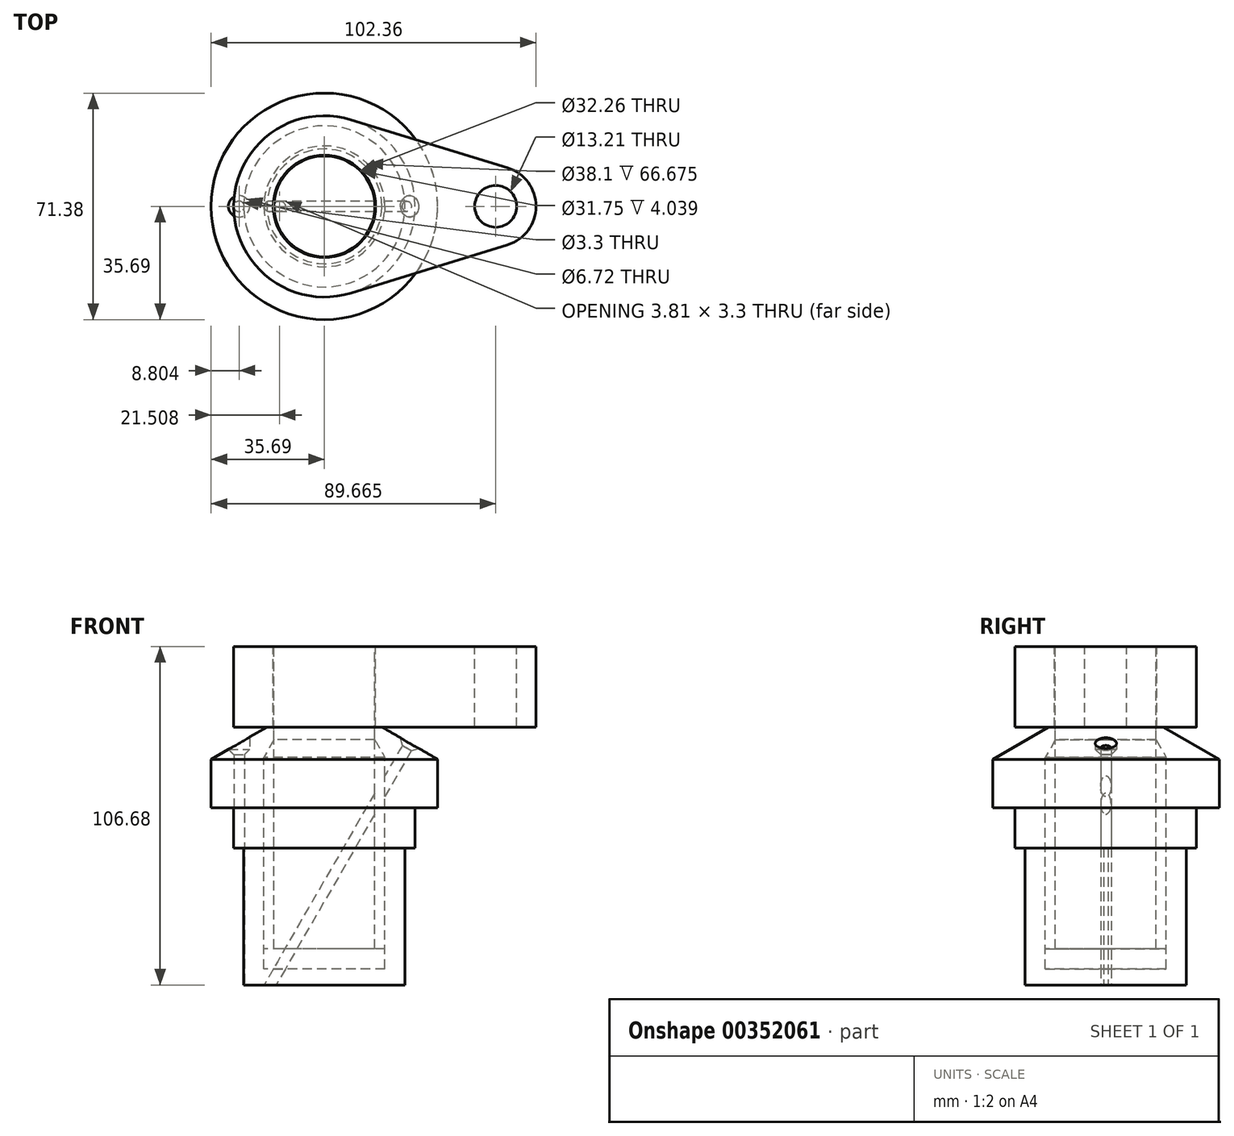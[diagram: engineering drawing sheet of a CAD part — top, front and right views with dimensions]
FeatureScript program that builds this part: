
annotation { "Feature Type Name" : "Feature", "Feature Type Description" : "" }
export const myFeature = defineFeature(function(context is Context, id is Id, definition is map)
    precondition{}
    {
        {
            var Q0;
            Q0=qCreatedBy(makeId("Front.planeOp"),FACE);
            var sketch = newSketch(context, id + "F0", { "sketchPlane" : qUnion([Q0])});
            skLineSegment(sketch, "E0", {"start": v(0, 0) * mm, "end": v(25.4, 0) * mm});
            skLineSegment(sketch, "E1", {"start": v(25.4, 0) * mm, "end": v(25.4, 43.2) * mm});
            skLineSegment(sketch, "E2", {"start": v(25.4, 43.2) * mm, "end": v(28.58, 43.2) * mm});
            skLineSegment(sketch, "E3", {"start": v(28.58, 43.2) * mm, "end": v(28.58, 55.9) * mm});
            skLineSegment(sketch, "E4", {"start": v(28.58, 55.9) * mm, "end": v(35.69, 55.9) * mm});
            skLineSegment(sketch, "E5", {"start": v(35.69, 55.9) * mm, "end": v(35.69, 71.13) * mm});
            skLineSegment(sketch, "E6", {"start": v(35.69, 71.13) * mm, "end": v(18.08, 81.3) * mm});
            skLineSegment(sketch, "E7", {"start": v(18.08, 81.3) * mm, "end": v(0, 81.3) * mm});
            skLineSegment(sketch, "E8", {"start": v(0, 81.3) * mm, "end": v(0, 0) * mm});
            skLineSegment(sketch, "E9", {"start": v(15.87, 81.3) * mm, "end": v(15.87, 77.25) * mm});
            skLineSegment(sketch, "E10", {"start": v(15.88, 77.25) * mm, "end": v(19.05, 71.75) * mm});
            skLineSegment(sketch, "E11", {"start": v(19.05, 71.75) * mm, "end": v(19.05, 5.08) * mm});
            skLineSegment(sketch, "E12", {"start": v(19.05, 5.08) * mm, "end": v(0, 5.08) * mm});
            skLineSegment(sketch, "E13", {"start": v(0, 89.12) * mm, "end": v(0, -8.25) * mm, "construction": true});
            skSolve(sketch);
        }
        {
            var Q0;
            {var subQ3=sQuery(id+"F0.wireOp",EDGE,"E0");Q0=makeQuery(id+"F0.imprint","IMPRINT",FACE,{"disambiguationData":[TD([[makeQuery(id+"F0.imprint","IMPRINT",EDGE,{"derivedFrom":subQ3}),1.0]])]});}
            var Q1;
            Q1=sQuery(id+"F0.wireOp",EDGE,"E8");
            revolve(context, id + "F1", {"entities" : qUnion([Q0]), "axis" : qUnion([Q1]), "revolveType" : RevolveType.FULL});
        }
        {
            var Q0;
            Q0=qCreatedBy(makeId("Front.planeOp"),FACE);
            var sketch = newSketch(context, id + "F2", { "sketchPlane" : qUnion([Q0])});
            skLineSegment(sketch, "E14.0", {"start": v(19.05, 5.08) * mm, "end": v(0, 5.08) * mm});
            skPoint(sketch, "E14.1", {"position": v(19.05, 11.43) * mm});
            skPoint(sketch, "E14.2", {"position": v(15.88, 77.25) * mm});
            skLineSegment(sketch, "E15", {"start": v(19.05, 5.08) * mm, "end": v(19.05, 11.43) * mm});
            skLineSegment(sketch, "E16", {"start": v(15.88, 11.43) * mm, "end": v(15.88, 106.68) * mm});
            skLineSegment(sketch, "E17", {"start": v(15.88, 106.68) * mm, "end": v(0, 106.68) * mm});
            skLineSegment(sketch, "E18", {"start": v(0, 106.68) * mm, "end": v(0, 5.08) * mm});
            skLineSegment(sketch, "E19", {"start": v(15.88, 11.43) * mm, "end": v(19.05, 11.43) * mm});
            skSolve(sketch);
        }
        {
            var Q0;
            Q0=makeQuery(id+"F2.imprint","IMPRINT",FACE,{"disambiguationData":[TD([[makeQuery(id+"F2.imprint","IMPRINT",EDGE,{"derivedFrom":sQuery(id+"F2.wireOp",EDGE,"E14.0")}),-1.0]])]});
            var Q1;
            Q1=sQuery(id+"F2.wireOp",EDGE,"E18");
            revolve(context, id + "F3", {"entities" : qUnion([Q0]), "axis" : qUnion([Q1]), "revolveType" : RevolveType.FULL});
        }
        {
            var Q0;
            Q0=makeQuery(id+"F3.opRevolve","SWEPT_FACE",FACE,{"disambiguationData":[OSD([sQuery(id+"F2.wireOp",EDGE,"E17")])]});
            var sketch = newSketch(context, id + "F4", { "sketchPlane" : qUnion([Q0])});
            skCircle(sketch, "E20", {"center": v(0, 0) * mm, "radius": 28.58 * mm});
            skCircle(sketch, "E21.0", {"center": v(0, 0) * mm, "radius": 15.88 * mm});
            skCircle(sketch, "E22", {"center": v(53.98, 0) * mm, "radius": 12.7 * mm});
            skLineSegment(sketch, "E23", {"start": v(8.4, 27.31) * mm, "end": v(57.71, 12.14) * mm});
            skLineSegment(sketch, "E24", {"start": v(8.4, -27.31) * mm, "end": v(57.71, -12.14) * mm});
            skCircle(sketch, "E25", {"center": v(0, 0) * mm, "radius": 16.13 * mm});
            skCircle(sketch, "E26", {"center": v(53.98, 0) * mm, "radius": 6.35 * mm});
            skCircle(sketch, "E27", {"center": v(53.98, 0) * mm, "radius": 6.6 * mm});
            skSolve(sketch);
        }
        {
            var Q0;
            Q0=makeQuery(id+"F1.opRevolve","SWEPT_FACE",FACE,{"disambiguationData":[OSD([sQuery(id+"F0.wireOp",EDGE,"E7")])]});
            cPlane(context, id + "F5", {"entities" : qUnion([Q0]), "cplaneType" : CPlaneType.OFFSET, "offset" : 3.8 * mm, "width" : 152.4 * mm, "height" : 152.4 * mm});
        }
        {
            var Q0;
            Q0=makeQuery(id+"F4.imprint","IMPRINT",FACE,{"disambiguationData":[TD([[makeQuery(id+"F4.imprint","IMPRINT",EDGE,{"derivedFrom":sQuery(id+"F4.wireOp",EDGE,"E25")}),-1.0]])]});
            var Q1;
            {var subQ0=sQuery(id+"F4.wireOp",EDGE,"E23");Q1=makeQuery(id+"F4.imprint","IMPRINT",FACE,{"disambiguationData":[TD([[makeQuery(id+"F4.imprint","IMPRINT",EDGE,{"derivedFrom":subQ0}),-1.0]])]});}
            var Q2;
            Q2=makeQuery(id+"F4.imprint","IMPRINT",FACE,{"disambiguationData":[TD([[makeQuery(id+"F4.imprint","IMPRINT",EDGE,{"derivedFrom":sQuery(id+"F4.wireOp",EDGE,"E27")}),-1.0]])]});
            var Q3;
            Q3=qCreatedBy(id+"F5.planeOp",FACE);
            extrude(context, id + "F6", {"entities" : qUnion([Q0, Q1, Q2]), "oppositeDirection" : true, "endBoundEntityFace" : qUnion([Q3]), "depth" : 25.4 * mm});
        }
        {
            var Q0;
            Q0=makeQuery(id+"F1.opRevolve","SWEPT_FACE",FACE,{"disambiguationData":[OSD([sQuery(id+"F0.wireOp",EDGE,"E7")])]});
            var sketch = newSketch(context, id + "F7", { "sketchPlane" : qUnion([Q0])});
            skLineSegment(sketch, "E28", {"start": v(-18.08, 0) * mm, "end": v(-35.69, 0) * mm, "construction": true});
            skPoint(sketch, "E29", {"position": v(-26.89, 0) * mm});
            skSolve(sketch);
        }
        {
            var Q0;
            Q0=sQuery(id+"F7.wireOp",VERTEX,"E29");
            var Q1;
            Q1=makeQuery(id+"F1.opRevolve","SWEPT_BODY",BODY,{"disambiguationData":[OSD([sQuery(id+"F0.wireOp",EDGE,"E0"),sQuery(id+"F0.wireOp",EDGE,"E1"),sQuery(id+"F0.wireOp",EDGE,"E2"),sQuery(id+"F0.wireOp",EDGE,"E3"),sQuery(id+"F0.wireOp",EDGE,"E4"),sQuery(id+"F0.wireOp",EDGE,"E5"),sQuery(id+"F0.wireOp",EDGE,"E6"),sQuery(id+"F0.wireOp",EDGE,"E7"),sQuery(id+"F0.wireOp",EDGE,"E8"),sQuery(id+"F0.wireOp",EDGE,"E9"),sQuery(id+"F0.wireOp",EDGE,"E10"),sQuery(id+"F0.wireOp",EDGE,"E11"),sQuery(id+"F0.wireOp",EDGE,"E12")])]});
            hole(context, id + "F8", {"style" : HoleStyle.C_SINK, "endStyle" : HoleEndStyle.THROUGH, "standardTappedOrClearance" : lookupTablePath({ "standard" : "ISO", "fit" : "Normal", "size" : "M3", "type" : "Clearance" }), "standardBlindInLast" : lookupTablePath({ "fit" : "Standard", "standard" : "ISO", "size" : "M3", "type" : "Clearance" }), "holeDiameter" : 3.3 * mm, "cSinkDiameter" : 6.72 * mm, "cSinkAngle" : 90 * degree, "isTappedThrough" : true, "tappedDepth" : 12.7 * mm, "tapClearance" : 3, "locations" : qUnion([Q0]), "scope" : qUnion([Q1]), "startStyle" : HoleStartStyle.PART});
        }
        {
            var Q0;
            Q0=qCreatedBy(makeId("Front.planeOp"),FACE);
            var sketch = newSketch(context, id + "F9", { "sketchPlane" : qUnion([Q0])});
            skLineSegment(sketch, "E30", {"start": v(18.08, 81.3) * mm, "end": v(35.69, 71.13) * mm, "construction": true});
            skPoint(sketch, "E31", {"position": v(26.89, 76.21) * mm});
            skSolve(sketch);
        }
        {
            var Q0;
            Q0=sQuery(id+"F9.wireOp",EDGE,"E30");
            cPlane(context, id + "F10", {"entities" : qUnion([Q0]), "cplaneType" : CPlaneType.LINE_ANGLE, "offset" : 25.4 * mm, "angle" : 90 * degree, "width" : 152.4 * mm, "height" : 152.4 * mm});
        }
        {
            var Q0;
            Q0=qCreatedBy(id+"F10.planeOp",FACE);
            var sketch = newSketch(context, id + "F11", { "sketchPlane" : qUnion([Q0])});
            skPoint(sketch, "E32.0", {"position": v(-14.82, 0) * mm});
            skSolve(sketch);
        }
        {
            var Q0;
            Q0=sQuery(id+"F11.wireOp",VERTEX,"E32.0");
            var Q1;
            Q1=makeQuery(id+"F1.opRevolve","SWEPT_BODY",BODY,{"disambiguationData":[OSD([sQuery(id+"F0.wireOp",EDGE,"E0"),sQuery(id+"F0.wireOp",EDGE,"E1"),sQuery(id+"F0.wireOp",EDGE,"E2"),sQuery(id+"F0.wireOp",EDGE,"E3"),sQuery(id+"F0.wireOp",EDGE,"E4"),sQuery(id+"F0.wireOp",EDGE,"E5"),sQuery(id+"F0.wireOp",EDGE,"E6"),sQuery(id+"F0.wireOp",EDGE,"E7"),sQuery(id+"F0.wireOp",EDGE,"E8"),sQuery(id+"F0.wireOp",EDGE,"E9"),sQuery(id+"F0.wireOp",EDGE,"E10"),sQuery(id+"F0.wireOp",EDGE,"E11"),sQuery(id+"F0.wireOp",EDGE,"E12")])]});
            var Q2;
            Q2=makeQuery(id+"F3.opRevolve","SWEPT_BODY",BODY,{"disambiguationData":[OSD([sQuery(id+"F2.wireOp",EDGE,"E14.0"),sQuery(id+"F2.wireOp",EDGE,"E15"),sQuery(id+"F2.wireOp",EDGE,"E16"),sQuery(id+"F2.wireOp",EDGE,"E17"),sQuery(id+"F2.wireOp",EDGE,"E18"),sQuery(id+"F2.wireOp",EDGE,"E19")])]});
            hole(context, id + "F12", {"style" : HoleStyle.C_SINK, "endStyle" : HoleEndStyle.THROUGH, "standardTappedOrClearance" : lookupTablePath({ "standard" : "ISO", "fit" : "Normal", "size" : "M3", "type" : "Clearance" }), "standardBlindInLast" : lookupTablePath({ "fit" : "Standard", "standard" : "ISO", "size" : "M3", "type" : "Clearance" }), "holeDiameter" : 3.3 * mm, "cSinkDiameter" : 6.72 * mm, "cSinkAngle" : 90 * degree, "isTappedThrough" : true, "tappedDepth" : 12.7 * mm, "tapClearance" : 3, "locations" : qUnion([Q0]), "scope" : qUnion([Q1, Q2]), "startStyle" : HoleStartStyle.PART});
        }
    });
